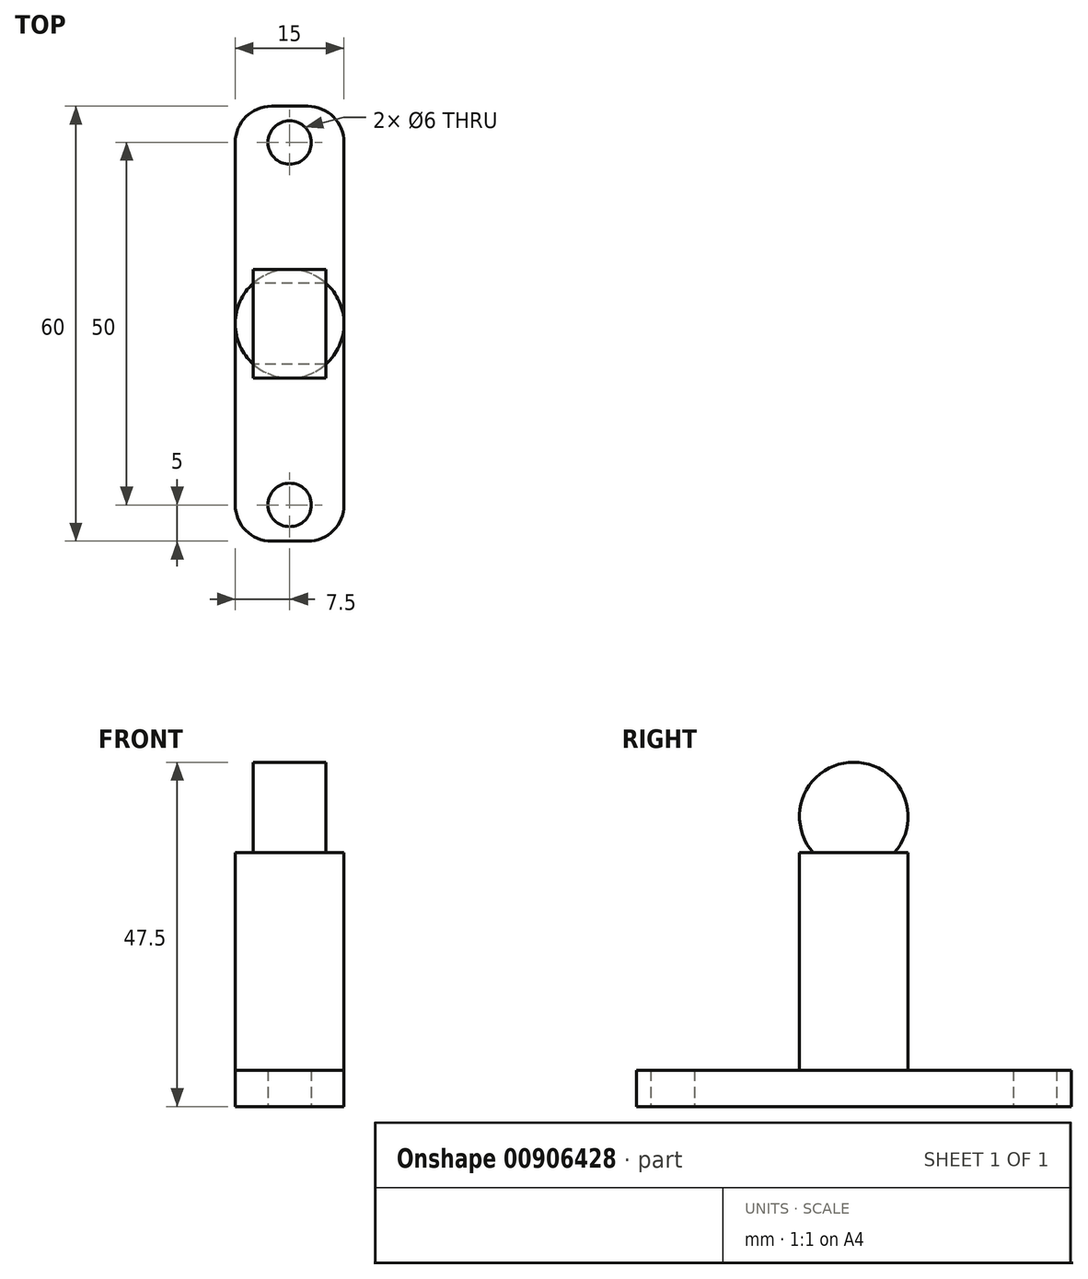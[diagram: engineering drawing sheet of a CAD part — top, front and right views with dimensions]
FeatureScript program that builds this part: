
annotation { "Feature Type Name" : "Feature", "Feature Type Description" : "" }
export const myFeature = defineFeature(function(context is Context, id is Id, definition is map)
    precondition{}
    {
        {
            var Q0;
            Q0=qCreatedBy(makeId("Top.planeOp"),FACE);
            var sketch = newSketch(context, id + "F0", { "sketchPlane" : qUnion([Q0])});
            skLineSegment(sketch, "E0.bottom", {"start": v(-7.5, -30) * mm, "end": v(7.5, -30) * mm});
            skLineSegment(sketch, "E0.top", {"start": v(-7.5, 30) * mm, "end": v(7.5, 30) * mm});
            skLineSegment(sketch, "E0.left", {"start": v(-7.5, -30) * mm, "end": v(-7.5, 30) * mm});
            skLineSegment(sketch, "E0.right", {"start": v(7.5, -30) * mm, "end": v(7.5, 30) * mm});
            skLineSegment(sketch, "E1", {"start": v(0, 30) * mm, "end": v(0, -30) * mm, "construction": true});
            skLineSegment(sketch, "E2", {"start": v(-7.5, 0) * mm, "end": v(7.5, 0) * mm, "construction": true});
            skSolve(sketch);
        }
        {
            var Q0;
            Q0 = qSketchRegion(id + "F0", true);
            extrude(context, id + "F1", {"entities" : qUnion([Q0]), "depth" : 5 * mm, "offsetDistance" : 25 * mm});
        }
        {
            var Q0;
            Q0=makeQuery(id+"F1.opExtrude","SWEPT_EDGE",EDGE,{"disambiguationData":[OSD([sQuery(id+"F0.wireOp",EDGE,"E0.top"),sQuery(id+"F0.wireOp",EDGE,"E0.left")])]});
            var Q1;
            Q1=makeQuery(id+"F1.opExtrude","SWEPT_EDGE",EDGE,{"disambiguationData":[OSD([sQuery(id+"F0.wireOp",EDGE,"E0.top"),sQuery(id+"F0.wireOp",EDGE,"E0.right")])]});
            var Q2;
            Q2=makeQuery(id+"F1.opExtrude","SWEPT_EDGE",EDGE,{"disambiguationData":[OSD([sQuery(id+"F0.wireOp",EDGE,"E0.bottom"),sQuery(id+"F0.wireOp",EDGE,"E0.right")])]});
            var Q3;
            Q3=makeQuery(id+"F1.opExtrude","SWEPT_EDGE",EDGE,{"disambiguationData":[OSD([sQuery(id+"F0.wireOp",EDGE,"E0.bottom"),sQuery(id+"F0.wireOp",EDGE,"E0.left")])]});
            fillet(context, id + "F2", {"entities" : qUnion([Q0, Q1, Q2, Q3]), "radius" : 5 * mm, "tangentPropagation" : true, "allowEdgeOverflow" : false});
        }
        {
            var Q0;
            Q0=makeQuery(id+"F1.opExtrude","CAP_FACE",FACE,{"disambiguationData":[OSD([sQuery(id+"F0.wireOp",EDGE,"E0.bottom"),sQuery(id+"F0.wireOp",EDGE,"E0.top"),sQuery(id+"F0.wireOp",EDGE,"E0.left"),sQuery(id+"F0.wireOp",EDGE,"E0.right")])],"isStart":false});
            var sketch = newSketch(context, id + "F3", { "sketchPlane" : qUnion([Q0])});
            skLineSegment(sketch, "E3", {"start": v(0, 30) * mm, "end": v(0, -30) * mm, "construction": true});
            skLineSegment(sketch, "E4", {"start": v(7.5, 0) * mm, "end": v(-7.5, 0) * mm, "construction": true});
            skCircle(sketch, "E5", {"center": v(0, 0) * mm, "radius": 7.5 * mm});
            skSolve(sketch);
        }
        {
            var Q0;
            Q0 = qSketchRegion(id + "F3", true);
            extrude(context, id + "F4", {"entities" : qUnion([Q0]), "operationType" : NewBodyOperationType.ADD, "depth" : 30 * mm, "offsetDistance" : 25 * mm});
        }
        {
            var Q0;
            Q0=makeQuery(id+"F1.opExtrude","CAP_FACE",FACE,{"disambiguationData":[OSD([sQuery(id+"F0.wireOp",EDGE,"E0.bottom"),sQuery(id+"F0.wireOp",EDGE,"E0.top"),sQuery(id+"F0.wireOp",EDGE,"E0.left"),sQuery(id+"F0.wireOp",EDGE,"E0.right")])],"isStart":true});
            var sketch = newSketch(context, id + "F5", { "sketchPlane" : qUnion([Q0])});
            skLineSegment(sketch, "E6", {"start": v(0, 30) * mm, "end": v(0, -30) * mm, "construction": true});
            skCircle(sketch, "E7", {"center": v(0, 25) * mm, "radius": 3 * mm});
            skCircle(sketch, "E8", {"center": v(0, -25) * mm, "radius": 3 * mm});
            skLineSegment(sketch, "E9", {"start": v(7.5, 0) * mm, "end": v(-7.5, 0) * mm, "construction": true});
            skSolve(sketch);
        }
        {
            var Q0;
            Q0=makeQuery(id+"F5.imprint","IMPRINT",FACE,{"disambiguationData":[TD([[makeQuery(id+"F5.imprint","IMPRINT",EDGE,{"derivedFrom":sQuery(id+"F5.wireOp",EDGE,"E8")}),1.0]])]});
            var Q1;
            Q1=makeQuery(id+"F5.imprint","IMPRINT",FACE,{"disambiguationData":[TD([[makeQuery(id+"F5.imprint","IMPRINT",EDGE,{"derivedFrom":sQuery(id+"F5.wireOp",EDGE,"E7")}),1.0]])]});
            extrude(context, id + "F6", {"entities" : qUnion([Q0, Q1]), "operationType" : NewBodyOperationType.REMOVE, "endBound" : BoundingType.UP_TO_NEXT, "oppositeDirection" : true, "depth" : 25 * mm, "offsetDistance" : 25 * mm});
        }
        {
            var Q0;
            Q0=qCreatedBy(makeId("Right.planeOp"),FACE);
            var sketch = newSketch(context, id + "F7", { "sketchPlane" : qUnion([Q0])});
            skCircle(sketch, "E10", {"center": v(0, 40) * mm, "radius": 7.5 * mm});
            skSolve(sketch);
        }
        {
            var Q0;
            Q0 = qSketchRegion(id + "F7", true);
            extrude(context, id + "F8", {"entities" : qUnion([Q0]), "operationType" : NewBodyOperationType.ADD, "endBound" : BoundingType.SYMMETRIC, "depth" : 10 * mm, "offsetDistance" : 25 * mm});
        }
    });
